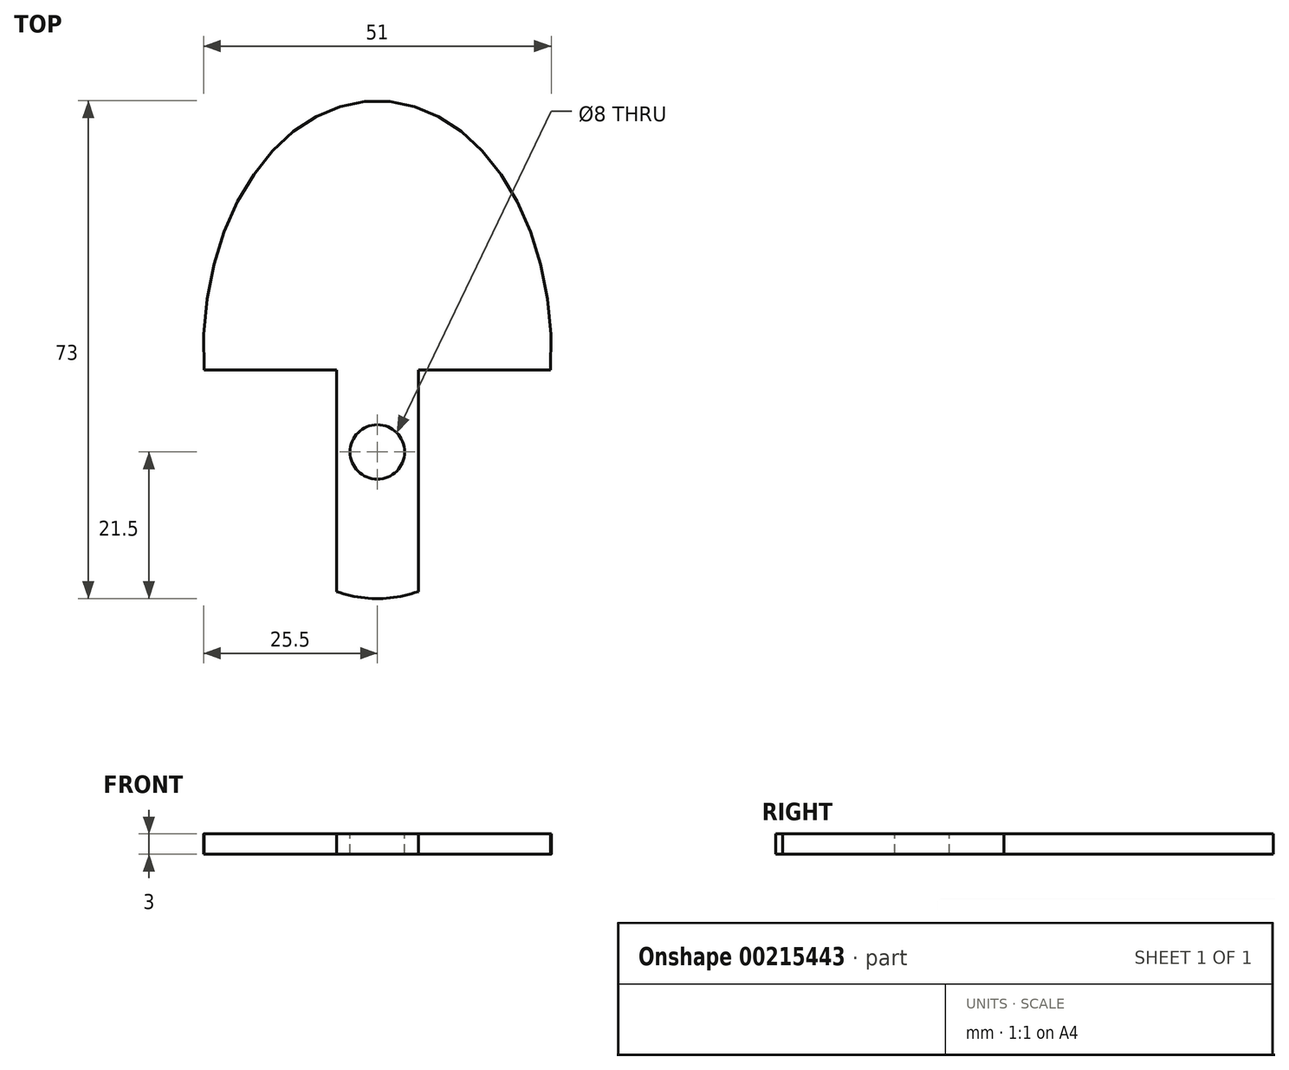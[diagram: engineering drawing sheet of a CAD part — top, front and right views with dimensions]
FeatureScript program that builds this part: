
annotation { "Feature Type Name" : "Feature", "Feature Type Description" : "" }
export const myFeature = defineFeature(function(context is Context, id is Id, definition is map)
    precondition{}
    {
        {
            var Q0;
            Q0=qCreatedBy(makeId("Top.planeOp"),FACE);
            var sketch = newSketch(context, id + "F0", { "sketchPlane" : qUnion([Q0])});
            skEllipse(sketch, "E0", {"center": v(0, 0) * mm, "majorRadius": 36.5 * mm, "minorRadius": 25.5 * mm, "majorAxis": v(0, 1)});
            skSolve(sketch);
        }
        {
            var Q0;
            Q0=makeQuery(id+"F0.imprint","IMPRINT",FACE,{"disambiguationData":[TD([[makeQuery(id+"F0.imprint","IMPRINT",EDGE,{"derivedFrom":sQuery(id+"F0.wireOp",EDGE,"E0")}),1.0]])]});
            extrude(context, id + "F1", {"entities" : qUnion([Q0]), "depth" : 3 * mm});
        }
        {
            var Q0;
            Q0=makeQuery(id+"F1.opExtrude","CAP_FACE",FACE,{"disambiguationData":[OSD([sQuery(id+"F0.wireOp",EDGE,"E0")])],"isStart":false});
            var sketch = newSketch(context, id + "F2", { "sketchPlane" : qUnion([Q0])});
            skCircle(sketch, "E1", {"center": v(0, -15) * mm, "radius": 4 * mm});
            skSolve(sketch);
        }
        {
            var Q0;
            Q0=makeQuery(id+"F2.imprint","IMPRINT",FACE,{"disambiguationData":[TD([[makeQuery(id+"F2.imprint","IMPRINT",EDGE,{"derivedFrom":sQuery(id+"F2.wireOp",EDGE,"E1")}),-1.0]])]});
            var sketch = newSketch(context, id + "F3", { "sketchPlane" : qUnion([Q0])});
            skLineSegment(sketch, "E2.bottom", {"start": v(-6, -3) * mm, "end": v(-36, -3) * mm});
            skLineSegment(sketch, "E2.top", {"start": v(-6, -43) * mm, "end": v(-36, -43) * mm});
            skLineSegment(sketch, "E2.left", {"start": v(-6, -3) * mm, "end": v(-6, -43) * mm});
            skLineSegment(sketch, "E2.right", {"start": v(-36, -3) * mm, "end": v(-36, -43) * mm});
            skLineSegment(sketch, "E3.bottom", {"start": v(6, -3) * mm, "end": v(36, -3) * mm});
            skLineSegment(sketch, "E3.top", {"start": v(6, -43) * mm, "end": v(36, -43) * mm});
            skLineSegment(sketch, "E3.left", {"start": v(6, -3) * mm, "end": v(6, -43) * mm});
            skLineSegment(sketch, "E3.right", {"start": v(36, -3) * mm, "end": v(36, -43) * mm});
            skSolve(sketch);
        }
        {
            var Q0;
            {var subQ0=sQuery(id+"F3.wireOp",EDGE,"E2.left");var subQ1=sQuery(id+"F3.wireOp",EDGE,"E2.bottom");var subQ2=makeQuery(id+"F3.imprint","INTERSECT",VERTEX,{"derivedFrom":[subQ1,subQ0]});Q0=makeQuery(id+"F3.imprint","IMPRINT",FACE,{"disambiguationData":[TD([[makeQuery(id+"F3.imprint","IMPRINT",EDGE,{"disambiguationData":[TD([[subQ2,-1.0]])],"derivedFrom":subQ1}),1.0]])]});}
            var Q1;
            {var subQ0=sQuery(id+"F3.wireOp",EDGE,"E3.left");var subQ1=sQuery(id+"F3.wireOp",EDGE,"E3.bottom");var subQ2=makeQuery(id+"F3.imprint","INTERSECT",VERTEX,{"derivedFrom":[subQ1,subQ0]});Q1=makeQuery(id+"F3.imprint","IMPRINT",FACE,{"disambiguationData":[TD([[makeQuery(id+"F3.imprint","IMPRINT",EDGE,{"disambiguationData":[TD([[subQ2,-1.0]])],"derivedFrom":subQ1}),-1.0]])]});}
            extrude(context, id + "F4", {"entities" : qUnion([Q0, Q1]), "operationType" : NewBodyOperationType.REMOVE, "oppositeDirection" : true, "depth" : 25 * mm});
        }
        {
            var Q0;
            Q0=makeQuery(id+"F2.imprint","IMPRINT",FACE,{"disambiguationData":[TD([[makeQuery(id+"F2.imprint","IMPRINT",EDGE,{"derivedFrom":sQuery(id+"F2.wireOp",EDGE,"E1")}),1.0]])]});
            var Q1;
            Q1=sQuery(id+"F2.wireOp",EDGE,"E1");
            extrude(context, id + "F5", {"entities" : qUnion([Q0]), "operationType" : NewBodyOperationType.REMOVE, "surfaceEntities" : qUnion([Q1]), "oppositeDirection" : true, "depth" : 25 * mm});
        }
    });
